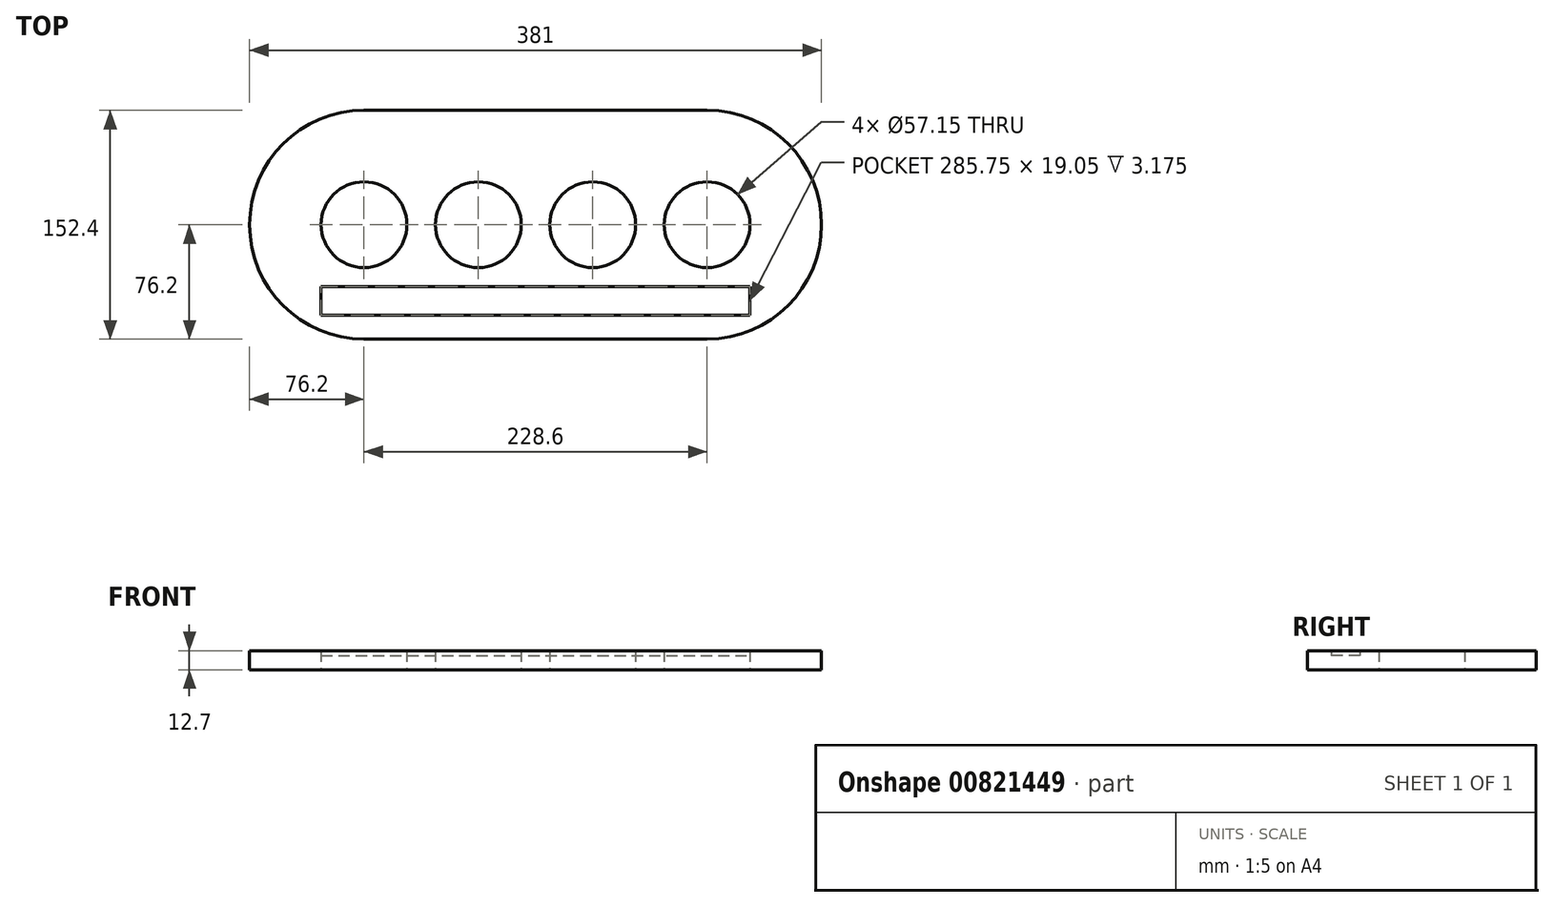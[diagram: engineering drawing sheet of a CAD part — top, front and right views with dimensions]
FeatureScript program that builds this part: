
annotation { "Feature Type Name" : "Feature", "Feature Type Description" : "" }
export const myFeature = defineFeature(function(context is Context, id is Id, definition is map)
    precondition{}
    {
        {
            var Q0;
            Q0=qCreatedBy(makeId("Top.planeOp"),FACE);
            var sketch = newSketch(context, id + "F0", { "sketchPlane" : qUnion([Q0])});
            skCircle(sketch, "E0", {"center": v(0, 0) * mm, "radius": 28.58 * mm});
            skCircle(sketch, "E1.1.0.0", {"center": v(76.2, 0) * mm, "radius": 28.58 * mm});
            skCircle(sketch, "E1.2.0.0", {"center": v(152.4, 0) * mm, "radius": 28.58 * mm});
            skCircle(sketch, "E1.3.0.0", {"center": v(228.6, 0) * mm, "radius": 28.58 * mm});
            skLineSegment(sketch, "E1.direction1", {"start": v(0, 0) * mm, "end": v(76.2, 0) * mm, "construction": true});
            skArc(sketch, "E2", {"start": v(0, 76.2) * mm, "mid": v(-76.2, 0) * mm, "end": v(0, -76.2) * mm});
            skLineSegment(sketch, "E3", {"start": v(0, 76.2) * mm, "end": v(228.6, 76.2) * mm});
            skLineSegment(sketch, "E4", {"start": v(228.6, -76.2) * mm, "end": v(0, -76.2) * mm});
            skArc(sketch, "E5.trimOffspring", {"start": v(228.6, -76.2) * mm, "mid": v(304.8, 0) * mm, "end": v(228.6, 76.2) * mm});
            skLineSegment(sketch, "E6.bottom", {"start": v(-28.57, -41.27) * mm, "end": v(257.18, -41.27) * mm});
            skLineSegment(sketch, "E6.top", {"start": v(-28.57, -60.32) * mm, "end": v(257.18, -60.32) * mm});
            skLineSegment(sketch, "E6.left", {"start": v(-28.57, -41.27) * mm, "end": v(-28.57, -60.32) * mm});
            skLineSegment(sketch, "E6.right", {"start": v(257.18, -41.27) * mm, "end": v(257.18, -60.32) * mm});
            skSolve(sketch);
        }
        {
            var Q0;
            Q0=makeQuery(id+"F0.imprint","IMPRINT",FACE,{"disambiguationData":[TD([[makeQuery(id+"F0.imprint","IMPRINT",EDGE,{"derivedFrom":sQuery(id+"F0.wireOp",EDGE,"E6.bottom")}),-1.0]])]});
            extrude(context, id + "F1", {"entities" : qUnion([Q0]), "depth" : 9.52 * mm, "offsetDistance" : 25.4 * mm});
        }
        {
            var Q0;
            Q0 = qSketchRegion(id + "F0", true);
            extrude(context, id + "F2", {"entities" : qUnion([Q0]), "operationType" : NewBodyOperationType.ADD, "depth" : 12.7 * mm, "offsetDistance" : 25.4 * mm});
        }
    });
